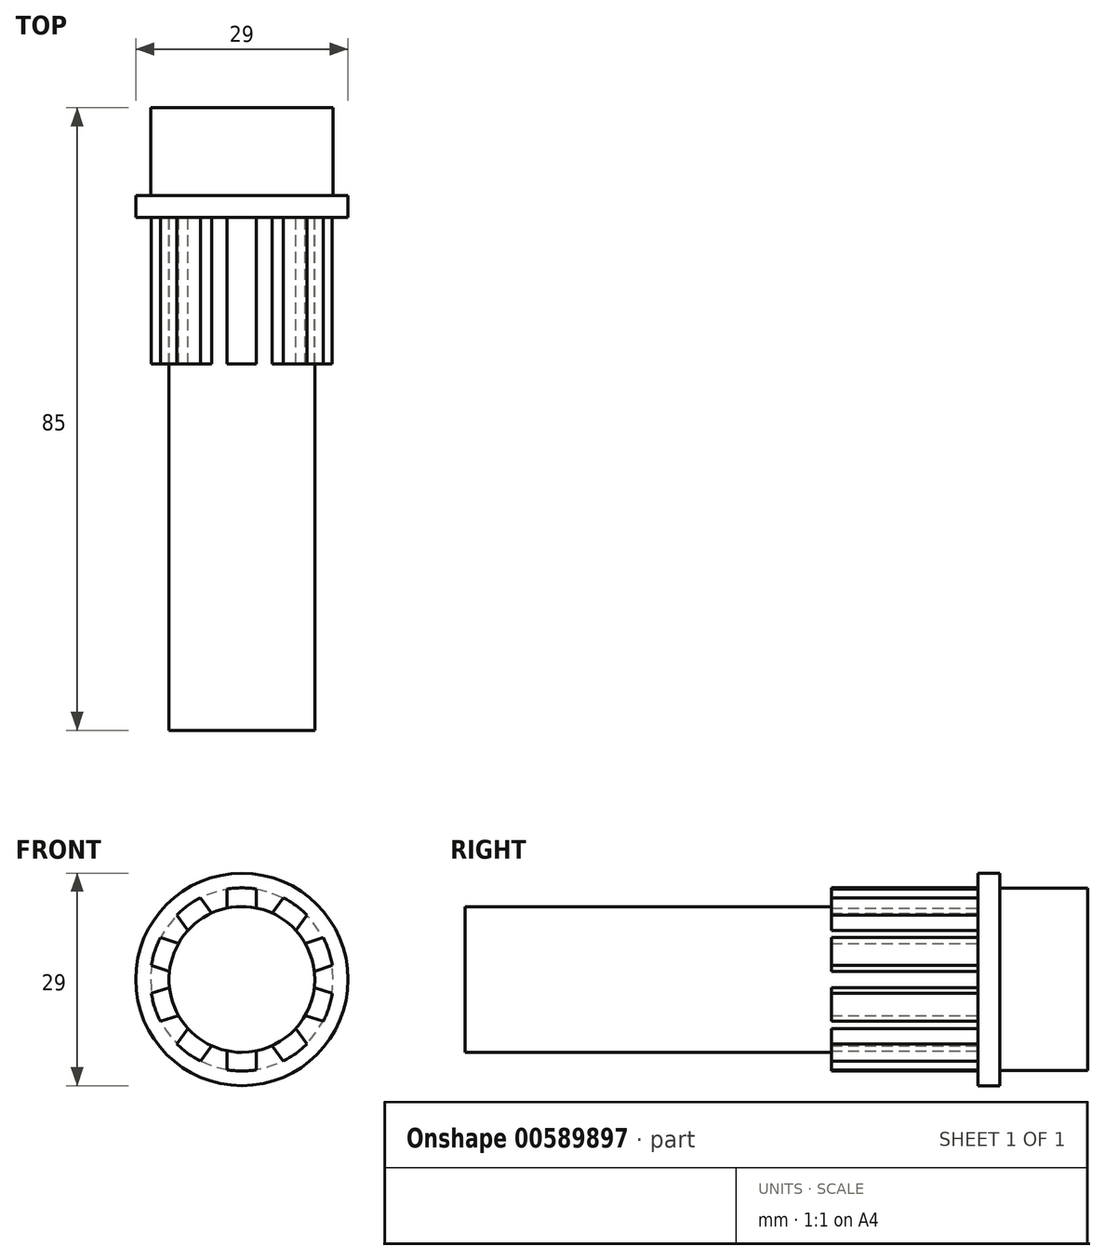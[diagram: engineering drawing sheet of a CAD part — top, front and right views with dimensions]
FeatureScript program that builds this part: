
annotation { "Feature Type Name" : "Feature", "Feature Type Description" : "" }
export const myFeature = defineFeature(function(context is Context, id is Id, definition is map)
    precondition{}
    {
        {
            var Q0;
            Q0=qCreatedBy(makeId("Front.planeOp"),FACE);
            var sketch = newSketch(context, id + "F0", { "sketchPlane" : qUnion([Q0])});
            skCircle(sketch, "E0", {"center": v(0, 0) * mm, "radius": 12.45 * mm});
            skSolve(sketch);
        }
        {
            var Q0;
            Q0 = qSketchRegion(id + "F0", true);
            extrude(context, id + "F1", {"entities" : qUnion([Q0]), "depth" : 12 * mm, "offsetDistance" : 25 * mm});
        }
        {
            var Q0;
            Q0=makeQuery(id+"F1.opExtrude","CAP_FACE",FACE,{"disambiguationData":[OSD([sQuery(id+"F0.wireOp",EDGE,"E0")])],"isStart":false});
            var sketch = newSketch(context, id + "F2", { "sketchPlane" : qUnion([Q0])});
            skCircle(sketch, "E1", {"center": v(0, 0) * mm, "radius": 14.5 * mm});
            skSolve(sketch);
        }
        {
            var Q0;
            Q0 = qSketchRegion(id + "F2", true);
            extrude(context, id + "F3", {"entities" : qUnion([Q0]), "operationType" : NewBodyOperationType.ADD, "depth" : 3 * mm, "offsetDistance" : 25 * mm});
        }
        {
            var Q0;
            Q0=makeQuery(id+"F3.opExtrude","CAP_FACE",FACE,{"disambiguationData":[OSD([sQuery(id+"F2.wireOp",EDGE,"E1")])],"isStart":false});
            var sketch = newSketch(context, id + "F4", { "sketchPlane" : qUnion([Q0])});
            skCircle(sketch, "E2", {"center": v(0, 0) * mm, "radius": 9.95 * mm});
            skSolve(sketch);
        }
        {
            var Q0;
            Q0 = qSketchRegion(id + "F4", true);
            extrude(context, id + "F5", {"entities" : qUnion([Q0]), "operationType" : NewBodyOperationType.ADD, "depth" : 70 * mm, "offsetDistance" : 25 * mm});
        }
        {
            var Q0;
            Q0=makeQuery(id+"F3.opExtrude","CAP_FACE",FACE,{"disambiguationData":[OSD([sQuery(id+"F2.wireOp",EDGE,"E1")])],"isStart":false});
            var sketch = newSketch(context, id + "F6", { "sketchPlane" : qUnion([Q0])});
            skArc(sketch, "E3", {"start": v(2, 12.34) * mm, "mid": v(0, 12.5) * mm, "end": v(-2, 12.34) * mm});
            skLineSegment(sketch, "E4", {"start": v(0, 13.22) * mm, "end": v(0, 9.01) * mm, "construction": true});
            skLineSegment(sketch, "E5", {"start": v(-2, 12.34) * mm, "end": v(-2, 9.6) * mm});
            skLineSegment(sketch, "E6", {"start": v(2, 12.34) * mm, "end": v(2, 8.96) * mm});
            skLineSegment(sketch, "E7.1.0", {"start": v(-5.63, 11.16) * mm, "end": v(-3.65, 8.42) * mm});
            skLineSegment(sketch, "E7.1.1", {"start": v(-8.87, 8.8) * mm, "end": v(-7.26, 6.6) * mm});
            skArc(sketch, "E7.1.2", {"start": v(-5.63, 11.16) * mm, "mid": v(-7.35, 10.11) * mm, "end": v(-8.87, 8.8) * mm});
            skLineSegment(sketch, "E7.2.0", {"start": v(-11.12, 5.72) * mm, "end": v(-7.9, 4.67) * mm});
            skLineSegment(sketch, "E7.2.1", {"start": v(-12.35, 1.91) * mm, "end": v(-9.75, 1.07) * mm});
            skArc(sketch, "E7.2.2", {"start": v(-11.12, 5.72) * mm, "mid": v(-11.89, 3.86) * mm, "end": v(-12.35, 1.91) * mm});
            skLineSegment(sketch, "E7.3.0", {"start": v(-12.35, -1.91) * mm, "end": v(-9.14, -0.87) * mm});
            skLineSegment(sketch, "E7.3.1", {"start": v(-11.12, -5.72) * mm, "end": v(-8.52, -4.87) * mm});
            skArc(sketch, "E7.3.2", {"start": v(-12.35, -1.91) * mm, "mid": v(-11.89, -3.86) * mm, "end": v(-11.12, -5.72) * mm});
            skLineSegment(sketch, "E7.4.0", {"start": v(-8.87, -8.8) * mm, "end": v(-6.88, -6.07) * mm});
            skLineSegment(sketch, "E7.4.1", {"start": v(-5.63, -11.16) * mm, "end": v(-4.03, -8.95) * mm});
            skArc(sketch, "E7.4.2", {"start": v(-8.87, -8.8) * mm, "mid": v(-7.35, -10.11) * mm, "end": v(-5.63, -11.16) * mm});
            skLineSegment(sketch, "E7.5.0", {"start": v(-2, -12.34) * mm, "end": v(-2, -8.96) * mm});
            skLineSegment(sketch, "E7.5.1", {"start": v(2, -12.34) * mm, "end": v(2, -9.6) * mm});
            skArc(sketch, "E7.5.2", {"start": v(-2, -12.34) * mm, "mid": v(0, -12.5) * mm, "end": v(2, -12.34) * mm});
            skLineSegment(sketch, "E7.6.0", {"start": v(5.63, -11.16) * mm, "end": v(3.65, -8.42) * mm});
            skLineSegment(sketch, "E7.6.1", {"start": v(8.87, -8.8) * mm, "end": v(7.26, -6.6) * mm});
            skArc(sketch, "E7.6.2", {"start": v(5.63, -11.16) * mm, "mid": v(7.35, -10.11) * mm, "end": v(8.87, -8.8) * mm});
            skLineSegment(sketch, "E7.7.0", {"start": v(11.12, -5.72) * mm, "end": v(7.9, -4.67) * mm});
            skLineSegment(sketch, "E7.7.1", {"start": v(12.35, -1.91) * mm, "end": v(9.75, -1.07) * mm});
            skArc(sketch, "E7.7.2", {"start": v(11.12, -5.72) * mm, "mid": v(11.89, -3.86) * mm, "end": v(12.35, -1.91) * mm});
            skLineSegment(sketch, "E7.8.0", {"start": v(12.35, 1.91) * mm, "end": v(9.14, 0.87) * mm});
            skLineSegment(sketch, "E7.8.1", {"start": v(11.12, 5.72) * mm, "end": v(8.52, 4.87) * mm});
            skArc(sketch, "E7.8.2", {"start": v(12.35, 1.91) * mm, "mid": v(11.89, 3.86) * mm, "end": v(11.12, 5.72) * mm});
            skLineSegment(sketch, "E7.9.0", {"start": v(8.87, 8.8) * mm, "end": v(6.88, 6.07) * mm});
            skLineSegment(sketch, "E7.9.1", {"start": v(5.63, 11.16) * mm, "end": v(4.03, 8.95) * mm});
            skArc(sketch, "E7.9.2", {"start": v(8.87, 8.8) * mm, "mid": v(7.35, 10.11) * mm, "end": v(5.63, 11.16) * mm});
            skSolve(sketch);
        }
        {
            var Q0;
            Q0 = qSketchRegion(id + "F6", true);
            var Q1;
            {var subQ0=sQuery(id+"F6.wireOp",EDGE,"E3");Q1=makeQuery(id+"F6.imprint","IMPRINT",FACE,{"disambiguationData":[TD([[makeQuery(id+"F6.imprint","IMPRINT",EDGE,{"derivedFrom":subQ0}),1.0]])]});}
            var Q2;
            {var subQ0=sQuery(id+"F6.wireOp",EDGE,"E7.1.2");Q2=makeQuery(id+"F6.imprint","IMPRINT",FACE,{"disambiguationData":[TD([[makeQuery(id+"F6.imprint","IMPRINT",EDGE,{"derivedFrom":subQ0}),1.0]])]});}
            var Q3;
            {var subQ0=sQuery(id+"F6.wireOp",EDGE,"E7.2.2");Q3=makeQuery(id+"F6.imprint","IMPRINT",FACE,{"disambiguationData":[TD([[makeQuery(id+"F6.imprint","IMPRINT",EDGE,{"derivedFrom":subQ0}),1.0]])]});}
            var Q4;
            {var subQ0=sQuery(id+"F6.wireOp",EDGE,"E7.3.2");Q4=makeQuery(id+"F6.imprint","IMPRINT",FACE,{"disambiguationData":[TD([[makeQuery(id+"F6.imprint","IMPRINT",EDGE,{"derivedFrom":subQ0}),1.0]])]});}
            var Q5;
            {var subQ0=sQuery(id+"F6.wireOp",EDGE,"E7.4.2");Q5=makeQuery(id+"F6.imprint","IMPRINT",FACE,{"disambiguationData":[TD([[makeQuery(id+"F6.imprint","IMPRINT",EDGE,{"derivedFrom":subQ0}),1.0]])]});}
            var Q6;
            {var subQ0=sQuery(id+"F6.wireOp",EDGE,"E7.5.2");Q6=makeQuery(id+"F6.imprint","IMPRINT",FACE,{"disambiguationData":[TD([[makeQuery(id+"F6.imprint","IMPRINT",EDGE,{"derivedFrom":subQ0}),1.0]])]});}
            var Q7;
            {var subQ0=sQuery(id+"F6.wireOp",EDGE,"E7.6.2");Q7=makeQuery(id+"F6.imprint","IMPRINT",FACE,{"disambiguationData":[TD([[makeQuery(id+"F6.imprint","IMPRINT",EDGE,{"derivedFrom":subQ0}),1.0]])]});}
            var Q8;
            {var subQ0=sQuery(id+"F6.wireOp",EDGE,"E7.7.2");Q8=makeQuery(id+"F6.imprint","IMPRINT",FACE,{"disambiguationData":[TD([[makeQuery(id+"F6.imprint","IMPRINT",EDGE,{"derivedFrom":subQ0}),1.0]])]});}
            var Q9;
            {var subQ0=sQuery(id+"F6.wireOp",EDGE,"E7.8.2");Q9=makeQuery(id+"F6.imprint","IMPRINT",FACE,{"disambiguationData":[TD([[makeQuery(id+"F6.imprint","IMPRINT",EDGE,{"derivedFrom":subQ0}),1.0]])]});}
            var Q10;
            {var subQ0=sQuery(id+"F6.wireOp",EDGE,"E7.9.2");Q10=makeQuery(id+"F6.imprint","IMPRINT",FACE,{"disambiguationData":[TD([[makeQuery(id+"F6.imprint","IMPRINT",EDGE,{"derivedFrom":subQ0}),1.0]])]});}
            extrude(context, id + "F7", {"entities" : qUnion([Q0, Q1, Q2, Q3, Q4, Q5, Q6, Q7, Q8, Q9, Q10]), "operationType" : NewBodyOperationType.ADD, "depth" : 20 * mm, "offsetDistance" : 25 * mm});
        }
        {
            var Q0;
            Q0=qCreatedBy(makeId("Top.planeOp"),FACE);
            cPlane(context, id + "F8", {"entities" : qUnion([Q0]), "cplaneType" : CPlaneType.OFFSET, "offset" : 6 * mm, "width" : 150 * mm, "height" : 150 * mm});
        }
    });
